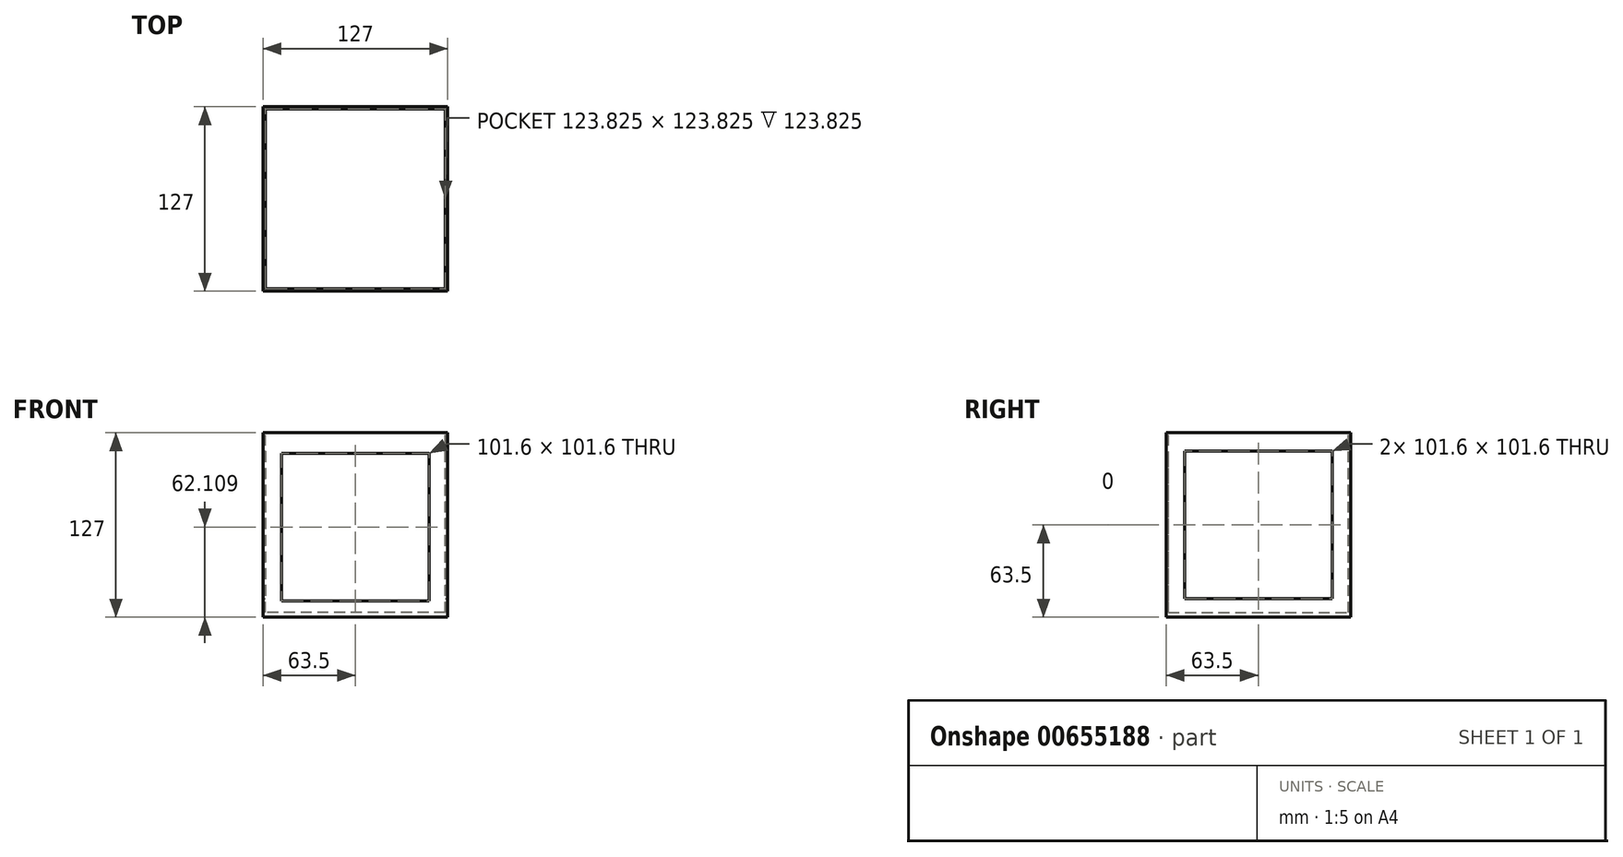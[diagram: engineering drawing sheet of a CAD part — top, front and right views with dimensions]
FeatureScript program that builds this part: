
annotation { "Feature Type Name" : "Feature", "Feature Type Description" : "" }
export const myFeature = defineFeature(function(context is Context, id is Id, definition is map)
    precondition{}
    {
        {
            var Q0;
            Q0=qCreatedBy(makeId("Front.planeOp"),FACE);
            var sketch = newSketch(context, id + "F0", { "sketchPlane" : qUnion([Q0])});
            skLineSegment(sketch, "E0.bottom", {"start": v(63.5, 63.5) * mm, "end": v(-63.5, 63.5) * mm});
            skLineSegment(sketch, "E0.top", {"start": v(63.5, -63.5) * mm, "end": v(-63.5, -63.5) * mm});
            skLineSegment(sketch, "E0.left", {"start": v(63.5, 63.5) * mm, "end": v(63.5, -63.5) * mm});
            skLineSegment(sketch, "E0.right", {"start": v(-63.5, 63.5) * mm, "end": v(-63.5, -63.5) * mm});
            skPoint(sketch, "E0.middle", {"position": v(0, 0) * mm});
            skSolve(sketch);
        }
        {
            var Q0;
            Q0 = qSketchRegion(id + "F0", true);
            extrude(context, id + "F1", {"entities" : qUnion([Q0]), "oppositeDirection" : true, "depth" : 127 * mm, "offsetDistance" : 25.4 * mm});
        }
        {
            var Q0;
            Q0=makeQuery(id+"F1.opExtrude","CAP_FACE",FACE,{"disambiguationData":[OSD([sQuery(id+"F0.wireOp",EDGE,"E0.bottom"),sQuery(id+"F0.wireOp",EDGE,"E0.top"),sQuery(id+"F0.wireOp",EDGE,"E0.left"),sQuery(id+"F0.wireOp",EDGE,"E0.right")])],"isStart":true});
            var sketch = newSketch(context, id + "F2", { "sketchPlane" : qUnion([Q0])});
            skLineSegment(sketch, "E1.bottom", {"start": v(50.8, -52.2) * mm, "end": v(-50.8, -52.2) * mm});
            skLineSegment(sketch, "E1.top", {"start": v(50.8, 49.4) * mm, "end": v(-50.8, 49.4) * mm});
            skLineSegment(sketch, "E1.left", {"start": v(50.8, -52.2) * mm, "end": v(50.8, 49.4) * mm});
            skLineSegment(sketch, "E1.right", {"start": v(-50.8, -52.2) * mm, "end": v(-50.8, 49.4) * mm});
            skPoint(sketch, "E1.middle", {"position": v(0, -1.4) * mm});
            skSolve(sketch);
        }
        {
            var Q0;
            Q0 = qSketchRegion(id + "F2", true);
            extrude(context, id + "F3", {"entities" : qUnion([Q0]), "operationType" : NewBodyOperationType.REMOVE, "oppositeDirection" : true, "depth" : 123.82 * mm, "offsetDistance" : 25.4 * mm});
        }
        {
            var Q0;
            Q0=makeQuery(id+"F1.opExtrude","SWEPT_FACE",FACE,{"disambiguationData":[OSD([sQuery(id+"F0.wireOp",EDGE,"E0.left")])]});
            var sketch = newSketch(context, id + "F4", { "sketchPlane" : qUnion([Q0])});
            skLineSegment(sketch, "E2.bottom", {"start": v(114.3, -50.8) * mm, "end": v(12.7, -50.8) * mm});
            skLineSegment(sketch, "E2.top", {"start": v(114.3, 50.8) * mm, "end": v(12.7, 50.8) * mm});
            skLineSegment(sketch, "E2.left", {"start": v(114.3, -50.8) * mm, "end": v(114.3, 50.8) * mm});
            skLineSegment(sketch, "E2.right", {"start": v(12.7, -50.8) * mm, "end": v(12.7, 50.8) * mm});
            skPoint(sketch, "E2.middle", {"position": v(63.5, 0) * mm});
            skPoint(sketch, "E2.middle.positionSnap0", {"position": v(0, 0) * mm});
            skPoint(sketch, "E2.centerSnap0", {"position": v(0, 0) * mm});
            skSolve(sketch);
        }
        {
            var Q0;
            Q0 = qSketchRegion(id + "F4", true);
            extrude(context, id + "F5", {"entities" : qUnion([Q0]), "operationType" : NewBodyOperationType.REMOVE, "endBound" : BoundingType.THROUGH_ALL, "oppositeDirection" : true, "depth" : 25.4 * mm, "offsetDistance" : 25.4 * mm});
        }
        {
            var Q0;
            Q0=makeQuery(id+"F1.opExtrude","SWEPT_FACE",FACE,{"disambiguationData":[OSD([sQuery(id+"F0.wireOp",EDGE,"E0.bottom")])]});
            var sketch = newSketch(context, id + "F6", { "sketchPlane" : qUnion([Q0])});
            skLineSegment(sketch, "E3", {"start": v(-63.5, 127) * mm, "end": v(0, 127) * mm});
            skLineSegment(sketch, "E4", {"start": v(0, 127) * mm, "end": v(0, 0) * mm, "construction": true});
            skLineSegment(sketch, "E5", {"start": v(0, 0) * mm, "end": v(-63.5, 0) * mm});
            skLineSegment(sketch, "E6", {"start": v(-63.5, 0) * mm, "end": v(-63.5, 63.5) * mm});
            skLineSegment(sketch, "E7", {"start": v(-63.5, 63.5) * mm, "end": v(63.5, 63.5) * mm, "construction": true});
            skLineSegment(sketch, "E8.bottom", {"start": v(61.91, 1.59) * mm, "end": v(-61.91, 1.59) * mm});
            skLineSegment(sketch, "E8.top", {"start": v(61.91, 125.41) * mm, "end": v(-61.91, 125.41) * mm});
            skLineSegment(sketch, "E8.left", {"start": v(61.91, 1.59) * mm, "end": v(61.91, 125.41) * mm});
            skLineSegment(sketch, "E8.right", {"start": v(-61.91, 1.59) * mm, "end": v(-61.91, 125.41) * mm});
            skPoint(sketch, "E8.middle", {"position": v(0, 63.5) * mm});
            skSolve(sketch);
        }
        {
            var Q0;
            Q0=makeQuery(id+"F6.imprint","IMPRINT",FACE,{"disambiguationData":[TD([[makeQuery(id+"F6.imprint","IMPRINT",EDGE,{"derivedFrom":sQuery(id+"F6.wireOp",EDGE,"E8.bottom")}),-1.0]])]});
            extrude(context, id + "F7", {"entities" : qUnion([Q0]), "operationType" : NewBodyOperationType.REMOVE, "oppositeDirection" : true, "depth" : 123.82 * mm, "offsetDistance" : 25.4 * mm});
        }
    });
